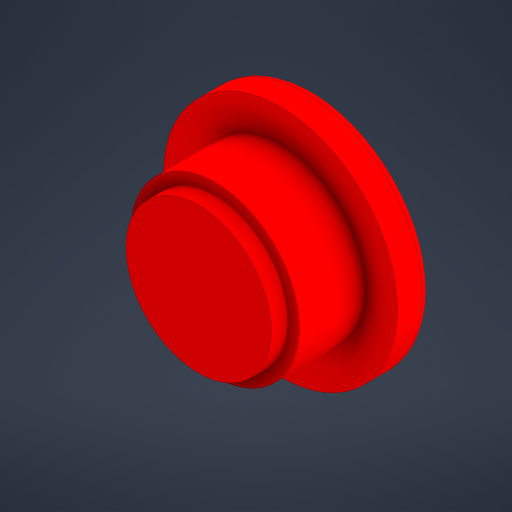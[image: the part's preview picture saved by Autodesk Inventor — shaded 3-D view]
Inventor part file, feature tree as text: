
AUTODESK INVENTOR PART (.ipt)
format: ipt  version: 2023.4 (Build 274418000, 418)  size: 282,112 bytes
history: native  units: mm
features: extrude x4, sketch x2, fillet x1, chamfer x1
ambient origin geometry x8: Origin, YZ Plane, XZ Plane, XY Plane, X Axis, Y Axis, Z Axis, Center Point
bodies: Solid1 (feature_tree)
feature tree (8):
  sketch  "Sketch1"  dims[d0=22.25mm d1=25.75mm]
  extrude  "Extrusion1"  Depth=25.75mm
  extrude  "Extrusion2"  Depth=5.0mm TaperAngle=0.0deg
  extrude  "Extrusion3"  Depth=10.0mm TaperAngle=0.0deg
  fillet  "Fillet1"  Radius=2.5mm
  extrude  "Extrusion4"  Depth=1.25mm
  chamfer  "Chamfer1"  Distance=25.0mm
  sketch  "Sketch2"  dims[d2=5.0mm d3=5.0mm d4=0.0mm d5=10.0mm d6=0.0mm d7=2.5mm d8=0.0mm d9=1.25mm d10=25.0mm d11=25.0mm d12=0.25mm d13=0.0mm d14=0.25mm d15=2.0mm d16=45.0deg]
